# Revit family: NeorestLS_S305_TUS
name_source: partatom
category: Plumbing Fixtures
revit_build: Autodesk Revit 2018 (Build: 20170223_1515(x64)
units: mm (PartAtom-declared; Revit-internal decimal feet)

## family parameters
Always vertical = Yes
Cut with Voids When Loaded = No
OmniClass Number = 23.45.00.00
OmniClass Title = Sanitary, Laundry, and Cleaning Equipment
Part Type = Normal
Room Calculation Point = No
Round Connector Dimension = Use Diameter
Shared = No
Work Plane-Based = No

## types (1)
- NeorestLS_S305_TUS
    CW Connection = Yes
    Description = SMART TOILET NEOREST LS
    Finish = White
    HW Connection = No
    Height = 529 mm  [stored 1.73556 ft]
    Length = 725 mm  [stored 2.37861 ft]
    Manufacturer = TOTO LTD.
    Material = Ceramic
    Model = MS8732CUMFG#01S（Remotecontroller:Silver）/MS8732CUMFG#01B（Remotecontroller:Black）/MS8732CUMFG#01N（Remotecontroller:Nickel）
    Rough-in = 305 mm  [stored 1.00066 ft]
    Seat Included = Yes
    URL = https://www.totousa.com
    Vent Connection = No
    Voltage = AC120V,60Hz
    Waste Connection = Yes
    Water Pressure = 0.05MPa～0.75MPa
    Water Use = 3.8L/3.0L
    Width = 411 mm  [stored 1.34843 ft]

note: [stored X ft] marks values corroborated as IEEE doubles in the binary element streams (Revit-internal decimal feet)

## geometry (parser evidence)
native form markers: Sweep x2
no freeform markers — native parametric forms only
